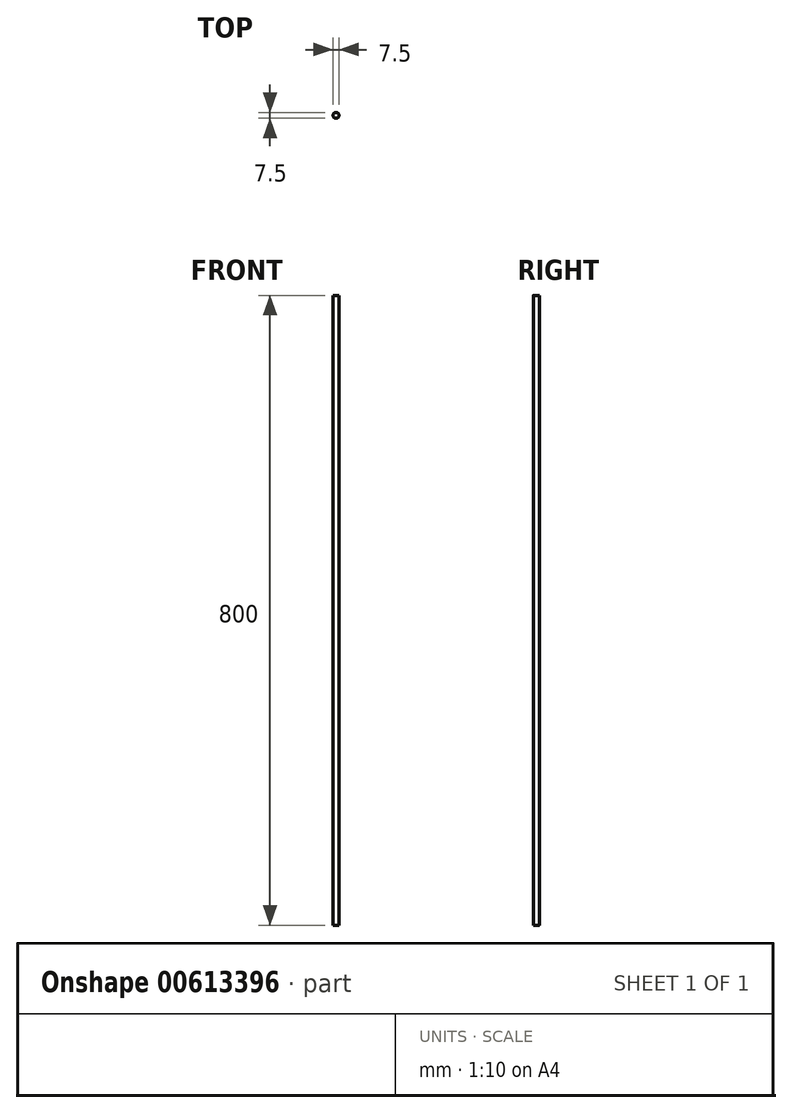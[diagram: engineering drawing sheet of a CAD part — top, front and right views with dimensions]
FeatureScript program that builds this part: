
annotation { "Feature Type Name" : "Feature", "Feature Type Description" : "" }
export const myFeature = defineFeature(function(context is Context, id is Id, definition is map)
    precondition{}
    {
        {
            var Q0;
            Q0=qCreatedBy(makeId("Top.planeOp"),FACE);
            var sketch = newSketch(context, id + "F0", { "sketchPlane" : qUnion([Q0])});
            skCircle(sketch, "E0", {"center": v(0, -0.54) * mm, "radius": 3.75 * mm});
            skSolve(sketch);
        }
        {
            var Q0;
            Q0=makeQuery(id+"F0.imprint","IMPRINT",FACE,{"disambiguationData":[TD([[makeQuery(id+"F0.imprint","IMPRINT",EDGE,{"derivedFrom":sQuery(id+"F0.wireOp",EDGE,"E0")}),1.0]])]});
            extrude(context, id + "F1", {"entities" : qUnion([Q0]), "depth" : 800 * mm, "offsetDistance" : 25 * mm});
        }
    });
